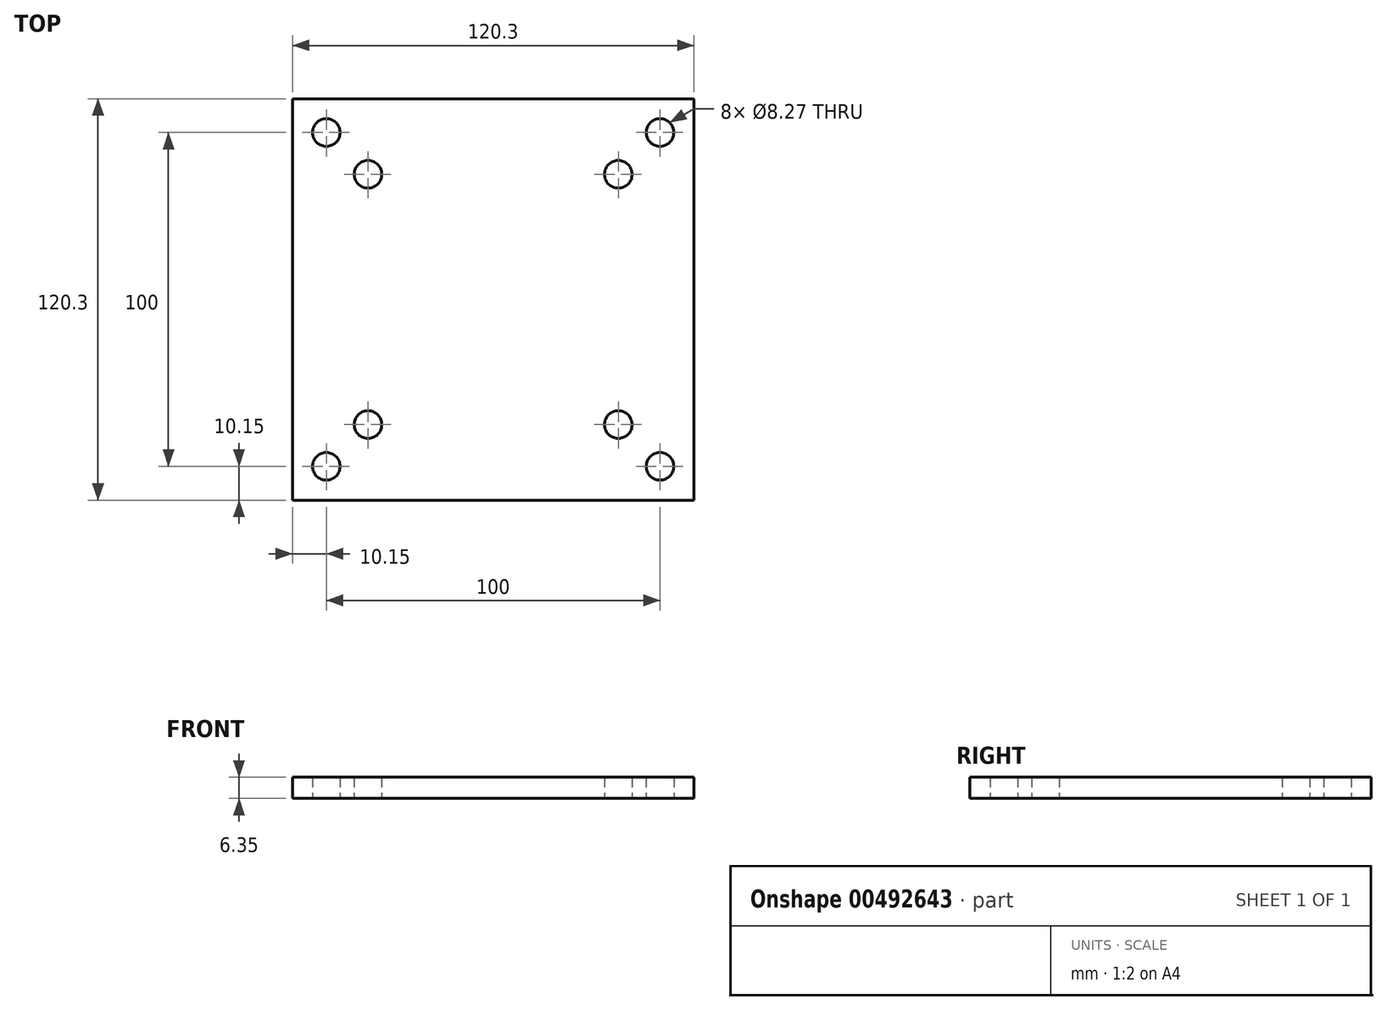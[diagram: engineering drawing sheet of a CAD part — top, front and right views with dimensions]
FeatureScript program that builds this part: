
annotation { "Feature Type Name" : "Feature", "Feature Type Description" : "" }
export const myFeature = defineFeature(function(context is Context, id is Id, definition is map)
    precondition{}
    {
        {
            var Q0;
            Q0=qCreatedBy(makeId("Top.planeOp"),FACE);
            var sketch = newSketch(context, id + "F0", { "sketchPlane" : qUnion([Q0])});
            skLineSegment(sketch, "E0.bottom", {"start": v(60.15, -60.15) * mm, "end": v(-60.15, -60.15) * mm});
            skLineSegment(sketch, "E0.top", {"start": v(60.15, 60.15) * mm, "end": v(-60.15, 60.15) * mm});
            skLineSegment(sketch, "E0.left", {"start": v(60.15, -60.15) * mm, "end": v(60.15, 60.15) * mm});
            skLineSegment(sketch, "E0.right", {"start": v(-60.15, -60.15) * mm, "end": v(-60.15, 60.15) * mm});
            skPoint(sketch, "E0.middle", {"position": v(0, 0) * mm});
            skLineSegment(sketch, "E1", {"start": v(0, 60.15) * mm, "end": v(0, -60.15) * mm, "construction": true});
            skLineSegment(sketch, "E2", {"start": v(-60.15, 0) * mm, "end": v(60.15, 0) * mm, "construction": true});
            skCircle(sketch, "E3", {"center": v(-50, 50) * mm, "radius": 4.14 * mm});
            skCircle(sketch, "E4.MirrorC", {"center": v(50, 50) * mm, "radius": 4.14 * mm});
            skCircle(sketch, "E5.MirrorC", {"center": v(-50, -50) * mm, "radius": 4.14 * mm});
            skCircle(sketch, "E6.MirrorC", {"center": v(50, -50) * mm, "radius": 4.14 * mm});
            skCircle(sketch, "E7", {"center": v(-37.5, 37.5) * mm, "radius": 4.14 * mm});
            skCircle(sketch, "E8.MirrorC", {"center": v(37.5, 37.5) * mm, "radius": 4.14 * mm});
            skCircle(sketch, "E9.MirrorC", {"center": v(-37.5, -37.5) * mm, "radius": 4.14 * mm});
            skCircle(sketch, "E10.MirrorC", {"center": v(37.5, -37.5) * mm, "radius": 4.14 * mm});
            skSolve(sketch);
        }
        {
            var Q0;
            Q0 = qSketchRegion(id + "F0", true);
            extrude(context, id + "F1", {"entities" : qUnion([Q0]), "depth" : 6.35 * mm});
        }
    });
